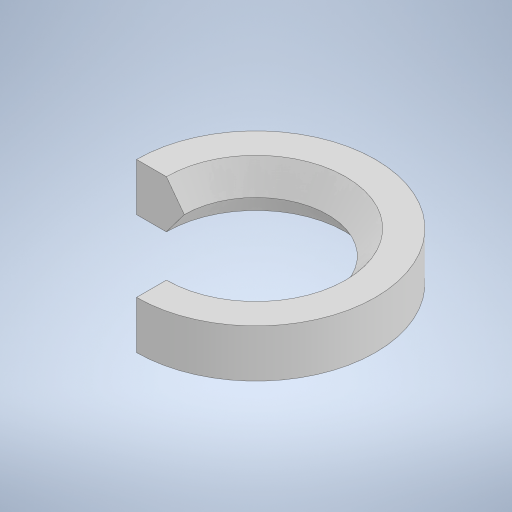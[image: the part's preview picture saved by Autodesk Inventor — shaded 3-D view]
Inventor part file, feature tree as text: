
AUTODESK INVENTOR PART (.ipt)
format: ipt  version: 2024 (Build 280153000, 153)  size: 244,736 bytes
history: native  units: mm
features: sketch x2, extrude x1, revolve x1
ambient origin geometry x8: Origin, YZ Plane, XZ Plane, XY Plane, X Axis, Y Axis, Z Axis, Center Point
bodies: Volumenkörper1 (feature_tree)
feature tree (4):
  extrude  "Extrusion1"  Depth=20.0mm
  revolve  "Umdrehung1"
  sketch  "Skizze1"  dims[d0=15.0mm d1=20.0mm]
  sketch  "Skizze2"  dims[d2=4.0mm d3=0.0mm d4=1.5mm d5=270.0deg]
